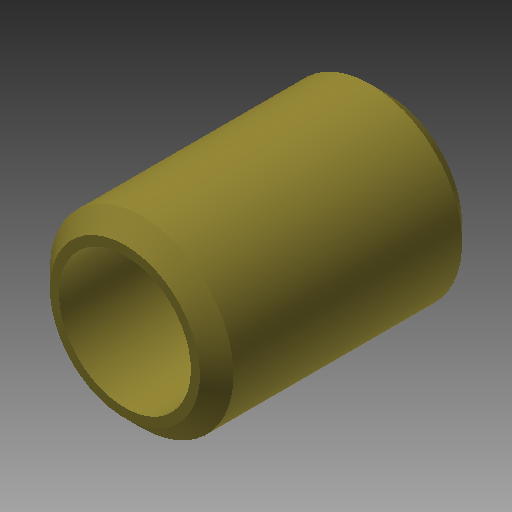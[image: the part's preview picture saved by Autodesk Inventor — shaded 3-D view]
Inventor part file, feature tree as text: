
AUTODESK INVENTOR PART (.ipt)
format: ipt  version: 2018 (Build 220112000, 112)  size: 137,728 bytes
history: native  units: in
note: dims shown in document units (in); Inventor stores cm internally (conversion verified against a paired STEP export)
features: other x35, revolve x1, sketch x1
ambient origin geometry x8: Origin, YZ Plane, XZ Plane, XY Plane, X Axis, Y Axis, Z Axis, Center Point
bodies: Solid1 (feature_tree)
feature tree (37):
  revolve  "Revolution1"  [1 undecoded]
  other  "bushing_XY"
  other  "bushing_YZ"
  other  "bushing_ZX"
  other  "bushing_X"
  other  "bushing_Y"
  other  "bushing_Z"
  other  "bushing_Center"
  other  "id1_XY"
  other  "id1_YZ"
  other  "id1_ZX"
  other  "id1_X"
  other  "id1_Y"
  other  "id1_Z"
  other  "id1_Center"
  other  "id2_XY"
  other  "id2_YZ"
  other  "id2_ZX"
  other  "id2_X"
  other  "id2_Y"
  other  "id2_Z"
  other  "id2_Center"
  other  "id3_XY"
  other  "id3_YZ"
  other  "id3_ZX"
  other  "id3_X"
  other  "id3_Y"
  other  "id3_Z"
  other  "id3_Center"
  other  "id4_XY"
  other  "id4_YZ"
  other  "id4_ZX"
  other  "id4_X"
  other  "id4_Y"
  other  "id4_Z"
  other  "id4_Center"
  sketch  "Sketch_1"  dims[d0=360.0deg d1=0.0in d2=0.0in]
note: 1 required parameter value undecoded (feature->parameter linkage not recoverable at this tier; creation-order binding heuristic only, values carry confidence <= 0.55)
